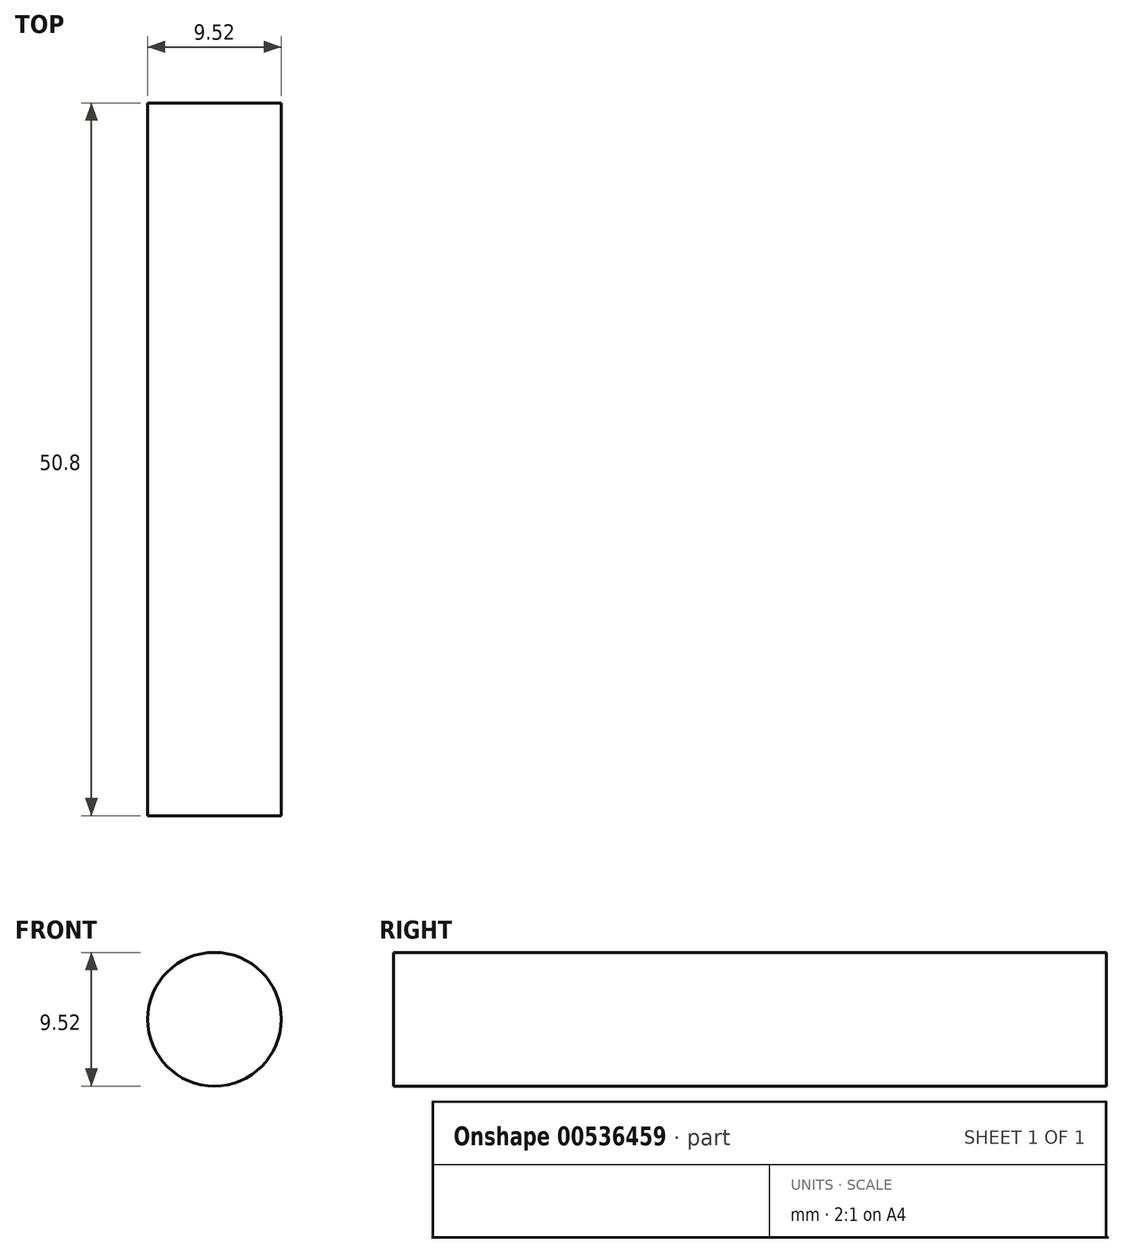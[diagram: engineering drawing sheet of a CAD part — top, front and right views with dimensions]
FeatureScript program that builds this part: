
annotation { "Feature Type Name" : "Feature", "Feature Type Description" : "" }
export const myFeature = defineFeature(function(context is Context, id is Id, definition is map)
    precondition{}
    {
        {
            var Q0;
            Q0=qCreatedBy(makeId("Front.planeOp"),FACE);
            var sketch = newSketch(context, id + "F0", { "sketchPlane" : qUnion([Q0])});
            skCircle(sketch, "E0", {"center": v(2.74, 7.53) * mm, "radius": 4.76 * mm});
            skSolve(sketch);
        }
        {
            var Q0;
            Q0=qSketchRegion(id+"F0",true);
            extrude(context, id + "F1", {"entities" : qUnion([Q0]), "depth" : 50.8 * mm, "offsetDistance" : 25.4 * mm});
        }
    });
